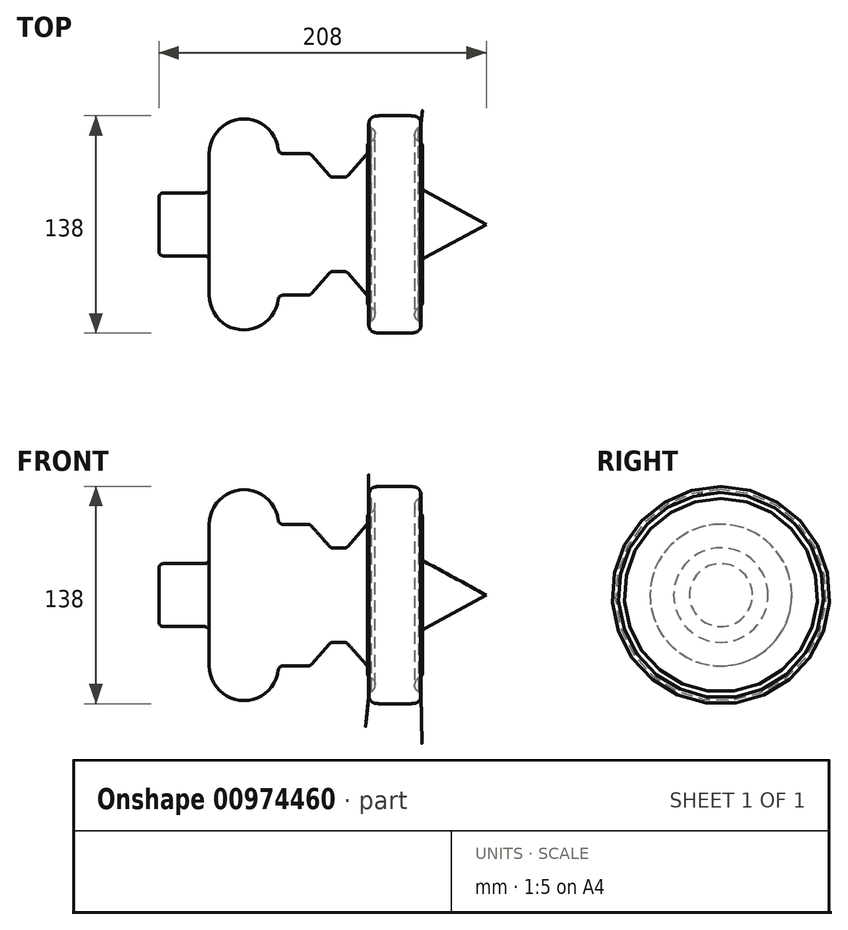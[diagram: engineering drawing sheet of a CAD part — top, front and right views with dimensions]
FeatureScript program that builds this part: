
annotation { "Feature Type Name" : "Feature", "Feature Type Description" : "" }
export const myFeature = defineFeature(function(context is Context, id is Id, definition is map)
    precondition{}
    {
        {
            var Q0;
            Q0=qCreatedBy(makeId("Front.planeOp"),FACE);
            var sketch = newSketch(context, id + "F0", { "sketchPlane" : qUnion([Q0])});
            skLineSegment(sketch, "E0", {"start": v(-156.91, 0) * mm, "end": v(109.43, 0) * mm, "construction": true});
            skLineSegment(sketch, "E1", {"start": v(-150, 0) * mm, "end": v(-150, 20) * mm});
            skLineSegment(sketch, "E2", {"start": v(-150, 20) * mm, "end": v(-118, 20) * mm});
            skLineSegment(sketch, "E3", {"start": v(-118, 20) * mm, "end": v(-118, 45) * mm});
            skArc(sketch, "E4", {"start": v(-118, 45) * mm, "mid": v(-96, 67) * mm, "end": v(-74, 45) * mm});
            skLineSegment(sketch, "E5", {"start": v(-74, 45) * mm, "end": v(-54, 45) * mm});
            skLineSegment(sketch, "E6", {"start": v(-54, 45) * mm, "end": v(-40.77, 30) * mm});
            skLineSegment(sketch, "E7", {"start": v(-40.77, 30) * mm, "end": v(-30.77, 30) * mm});
            skLineSegment(sketch, "E8", {"start": v(-30.77, 30) * mm, "end": v(-17.54, 45) * mm});
            skLineSegment(sketch, "E9", {"start": v(-17.54, 45) * mm, "end": v(-17.54, 52) * mm});
            skLineSegment(sketch, "E10", {"start": v(-17.54, 62) * mm, "end": v(-17.54, 69) * mm});
            skLineSegment(sketch, "E11", {"start": v(-17.54, 69) * mm, "end": v(17.46, 69) * mm});
            skLineSegment(sketch, "E12", {"start": v(17.46, 69) * mm, "end": v(17.46, 62) * mm});
            skLineSegment(sketch, "E13", {"start": v(17.46, 52) * mm, "end": v(17.46, 22) * mm});
            skLineSegment(sketch, "E14", {"start": v(17.46, 22) * mm, "end": v(58, 0) * mm});
            skLineSegment(sketch, "E15", {"start": v(58, 0) * mm, "end": v(-150, 0) * mm});
            skArc(sketch, "E16", {"start": v(-17.54, 52) * mm, "mid": v(-12.54, 57) * mm, "end": v(-17.54, 62) * mm});
            skArc(sketch, "E17", {"start": v(17.46, 62) * mm, "mid": v(12.46, 57) * mm, "end": v(17.46, 52) * mm});
            skSolve(sketch);
        }
        {
            var Q0;
            Q0 = qSketchRegion(id + "F0", true);
            var Q1;
            Q1=sQuery(id+"F0.wireOp",EDGE,"E0");
            revolve(context, id + "F1", {"surfaceOperationType" : NewSurfaceOperationType.NEW, "entities" : qUnion([Q0]), "axis" : qUnion([Q1]), "revolveType" : RevolveType.FULL});
        }
        {
            var Q0;
            Q0=makeQuery(id+"F1.opRevolve","SWEPT_EDGE",EDGE,{"disambiguationData":[OSD([sQuery(id+"F0.wireOp",EDGE,"E10"),sQuery(id+"F0.wireOp",EDGE,"E11")])]});
            var Q1;
            Q1=makeQuery(id+"F1.opRevolve","SWEPT_EDGE",EDGE,{"disambiguationData":[OSD([sQuery(id+"F0.wireOp",EDGE,"E11"),sQuery(id+"F0.wireOp",EDGE,"E12")])]});
            fillet(context, id + "F2", {"entities" : qUnion([Q0, Q1]), "radius" : 10 * mm, "tangentPropagation" : true, "rho" : 0.7, "crossSection" : FilletCrossSection.CONIC, "allowEdgeOverflow" : false});
        }
        {
            var Q0;
            Q0=makeQuery(id+"F1.opRevolve","SWEPT_EDGE",EDGE,{"disambiguationData":[OSD([sQuery(id+"F0.wireOp",EDGE,"E9"),sQuery(id+"F0.wireOp",EDGE,"E16")])]});
            var Q1;
            Q1=makeQuery(id+"F1.opRevolve","SWEPT_EDGE",EDGE,{"disambiguationData":[OSD([sQuery(id+"F0.wireOp",EDGE,"E8"),sQuery(id+"F0.wireOp",EDGE,"E9")])]});
            var Q2;
            Q2=makeQuery(id+"F2.opFillet","BLEND_EDGE",EDGE,{"blendedFrom":[makeQuery(id+"F1.opRevolve","SWEPT_EDGE",EDGE,{"disambiguationData":[OSD([sQuery(id+"F0.wireOp",EDGE,"E10"),sQuery(id+"F0.wireOp",EDGE,"E11")])]}),makeQuery(id+"F1.opRevolve","SWEPT_FACE",FACE,{"disambiguationData":[OSD([sQuery(id+"F0.wireOp",EDGE,"E16")])]})],"blendedInto":[makeQuery(id+"F1.opRevolve","SWEPT_FACE",FACE,{"disambiguationData":[OSD([sQuery(id+"F0.wireOp",EDGE,"E16")])]})]});
            var Q3;
            Q3=makeQuery(id+"F1.opRevolve","SWEPT_EDGE",EDGE,{"disambiguationData":[OSD([sQuery(id+"F0.wireOp",EDGE,"E5"),sQuery(id+"F0.wireOp",EDGE,"E6")])]});
            var Q4;
            Q4=makeQuery(id+"F1.opRevolve","SWEPT_EDGE",EDGE,{"disambiguationData":[OSD([sQuery(id+"F0.wireOp",EDGE,"E6"),sQuery(id+"F0.wireOp",EDGE,"E7")])]});
            var Q5;
            Q5=makeQuery(id+"F1.opRevolve","SWEPT_EDGE",EDGE,{"disambiguationData":[OSD([sQuery(id+"F0.wireOp",EDGE,"E7"),sQuery(id+"F0.wireOp",EDGE,"E8")])]});
            var Q6;
            Q6=makeQuery(id+"F1.opRevolve","SWEPT_EDGE",EDGE,{"disambiguationData":[OSD([sQuery(id+"F0.wireOp",EDGE,"E4"),sQuery(id+"F0.wireOp",EDGE,"E5")])]});
            var Q7;
            Q7=makeQuery(id+"F1.opRevolve","SWEPT_FACE",FACE,{"disambiguationData":[OSD([sQuery(id+"F0.wireOp",EDGE,"E13")])]});
            var Q8;
            Q8=makeQuery(id+"F2.opFillet","BLEND_EDGE",EDGE,{"blendedFrom":[makeQuery(id+"F1.opRevolve","SWEPT_EDGE",EDGE,{"disambiguationData":[OSD([sQuery(id+"F0.wireOp",EDGE,"E11"),sQuery(id+"F0.wireOp",EDGE,"E12")])]}),makeQuery(id+"F1.opRevolve","SWEPT_FACE",FACE,{"disambiguationData":[OSD([sQuery(id+"F0.wireOp",EDGE,"E17")])]})],"blendedInto":[makeQuery(id+"F1.opRevolve","SWEPT_FACE",FACE,{"disambiguationData":[OSD([sQuery(id+"F0.wireOp",EDGE,"E17")])]})]});
            var Q9;
            Q9=makeQuery(id+"F1.opRevolve","SWEPT_EDGE",EDGE,{"disambiguationData":[OSD([sQuery(id+"F0.wireOp",EDGE,"E1"),sQuery(id+"F0.wireOp",EDGE,"E2")])]});
            var Q10;
            Q10=makeQuery(id+"F1.opRevolve","SWEPT_EDGE",EDGE,{"disambiguationData":[OSD([sQuery(id+"F0.wireOp",EDGE,"E2"),sQuery(id+"F0.wireOp",EDGE,"E3")])]});
            fillet(context, id + "F3", {"entities" : qUnion([Q0, Q1, Q2, Q3, Q4, Q5, Q6, Q7, Q8, Q9, Q10]), "radius" : 3 * mm, "tangentPropagation" : true, "allowEdgeOverflow" : false});
        }
    });
